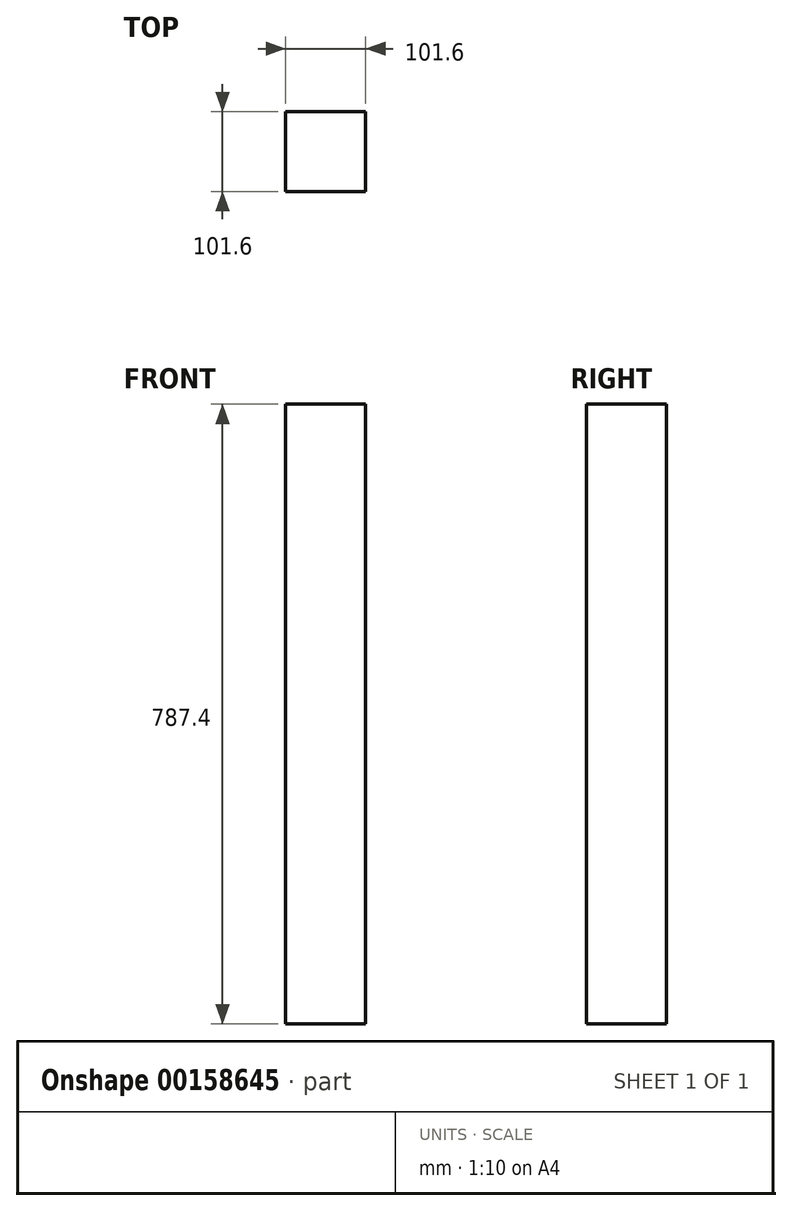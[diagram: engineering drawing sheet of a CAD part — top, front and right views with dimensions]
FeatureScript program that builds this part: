
annotation { "Feature Type Name" : "Feature", "Feature Type Description" : "" }
export const myFeature = defineFeature(function(context is Context, id is Id, definition is map)
    precondition{}
    {
        {
            var Q0;
            Q0=qCreatedBy(makeId("Top.planeOp"),FACE);
            var sketch = newSketch(context, id + "F0", { "sketchPlane" : qUnion([Q0])});
            skLineSegment(sketch, "E0.bottom", {"start": v(-30.69, 56.2) * mm, "end": v(70.91, 56.2) * mm});
            skLineSegment(sketch, "E0.top", {"start": v(-30.69, -45.4) * mm, "end": v(70.91, -45.4) * mm});
            skLineSegment(sketch, "E0.left", {"start": v(-30.69, 56.2) * mm, "end": v(-30.69, -45.4) * mm});
            skLineSegment(sketch, "E0.right", {"start": v(70.91, 56.2) * mm, "end": v(70.91, -45.4) * mm});
            skSolve(sketch);
        }
        {
            var Q0;
            Q0 = qSketchRegion(id + "F0", true);
            extrude(context, id + "F1", {"entities" : qUnion([Q0]), "oppositeDirection" : true, "depth" : 787.4 * mm});
        }
    });
